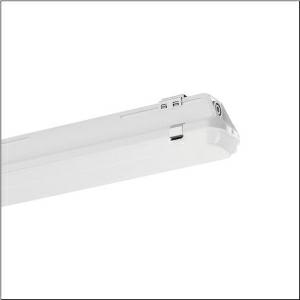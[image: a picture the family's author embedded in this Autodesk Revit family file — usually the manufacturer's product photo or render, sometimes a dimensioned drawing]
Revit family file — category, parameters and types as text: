
# Revit family: monsun_r__21_emergency_51fb107p487b3g_e760
name_source: partatom
category: Lighting Fixtures
units: mm (PartAtom-declared; Revit-internal decimal feet)

## family parameters
Cut with Voids When Loaded = No
Host = Face
Light Source = No
Part Type = Normal
Room Calculation Point = No
Round Connector Dimension = Use Diameter
Shared = No

## types (1)
- Monsun® 21 emergency (1 x LED, 8090 lm, 57.3 W, 4000K)
    Apparent Load = 57 VA
    CIE Flux Codes = 47 77 93 94 100
    Color Rendering = 80
    Color Temperature = 4000K
    Default Elevation = 1800 mm
    Description = Monsun® 21 emergency, damp-proof luminaire, chain hanger, primary optical cover: enclosure, of PMMA, light emission: direct distribution, primary light characteristic: symmetric, installation type: vertical mounting, horizontal mounting, surface-mounted, suspended mounting, LED, rated luminous flux: 8.090lm, luminous efficacy: 141lm/W, light colour: 840, colour temperature: 4000K, control gear: ECG, with terminal, 4-pole, max. 2.5mm², mains connection: 220..240V, AC, 50/60Hz, rated input power: 57W, control gear: single battery element, battery: NiCd, 4,5Ah, mains connection: 230V, housing, of glass-fibre reinforced polyester, uncoated, bright grey, length: 1.590mm, width: 90mm, height: 88mm, clip for enclosure, of stainless steel (V2A), ceiling mounting element, of stainless steel (V2A), chain hanger, of stainless steel (V2A), protection rating (complete): IP66, insulation class (complete): insulation class I (protective earthing), certification: CE, UKCA, protection symbol: D, impact resistance: IK04, permissible operating ambient temperature: +5..+25°C, standard: EN 60598-2-1, EN 50419, EN 60598-2-22, corresponds to IFS (International Featured Standards) requirements for safety and quality in the food industry, for indoor or canopied outdoor use, no direct snow, no direct sun, no direct rain, packaging unit: 1 piece
    Height = 89 mm
    Lamp = 1 x LED
    Lamp Light Flux = 8090 lm
    Lamp Power = 57.3 W
    Lamp count = 1
    Length = 1590 mm
    Luminous efficacy = 141 lm/W
    Manufacturer = Siteco
    ModVariant = No
    Model = 51FB107P487B3G
    Mounting Place = Ceiling
    Mounting Type = Pendant
    Number of Poles = 1
    OnlyDefault = Yes
    Power Factor = 1
    Product Name = Monsun® 21 emergency
    Product group = damp-proof luminaire | ceiling pendant
    ProductGroupID = 908
    Protection Class = Protection class I
    Protection Degree = IP 66
    RLX_Detail_Level = 1
    RlxData = <blob elided: 88589 chars, md5=53ea7825>
    Socket = socket
    Standby Power = 0 W
    System Light Flux = 8090 lm
    System Power = 57 W
    Type Comments = Product without accessories
    Type Image = l_1006717.jpg
    URL = http://relux.com
    VarID = ---
    Voltage = 0 V
    Weight = 0.00 kg
    Width = 90 mm

## geometry (parser evidence)
native form markers: Blend x4, Sweep x13
no freeform markers — native parametric forms only
